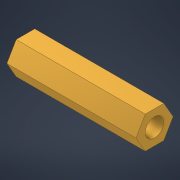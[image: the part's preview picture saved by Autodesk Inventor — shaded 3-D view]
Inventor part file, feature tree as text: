
AUTODESK INVENTOR PART (.ipt)
format: ipt  version: 2022 (Build 260153000, 153)  size: 97,792 bytes
history: native  units: mm
features: extrude x1, sketch x1
ambient origin geometry x8: Origin, YZ Plane, XZ Plane, XY Plane, X Axis, Y Axis, Z Axis, Center Point
bodies: Solid1 (feature_tree)
feature tree (2):
  extrude  "Extrusion1"  Depth=3.0mm
  sketch  "Sketch1"  dims[d0=6.0mm d1=3.0mm d2=20.866mm d3=0.0mm d4=5.196152mm]
